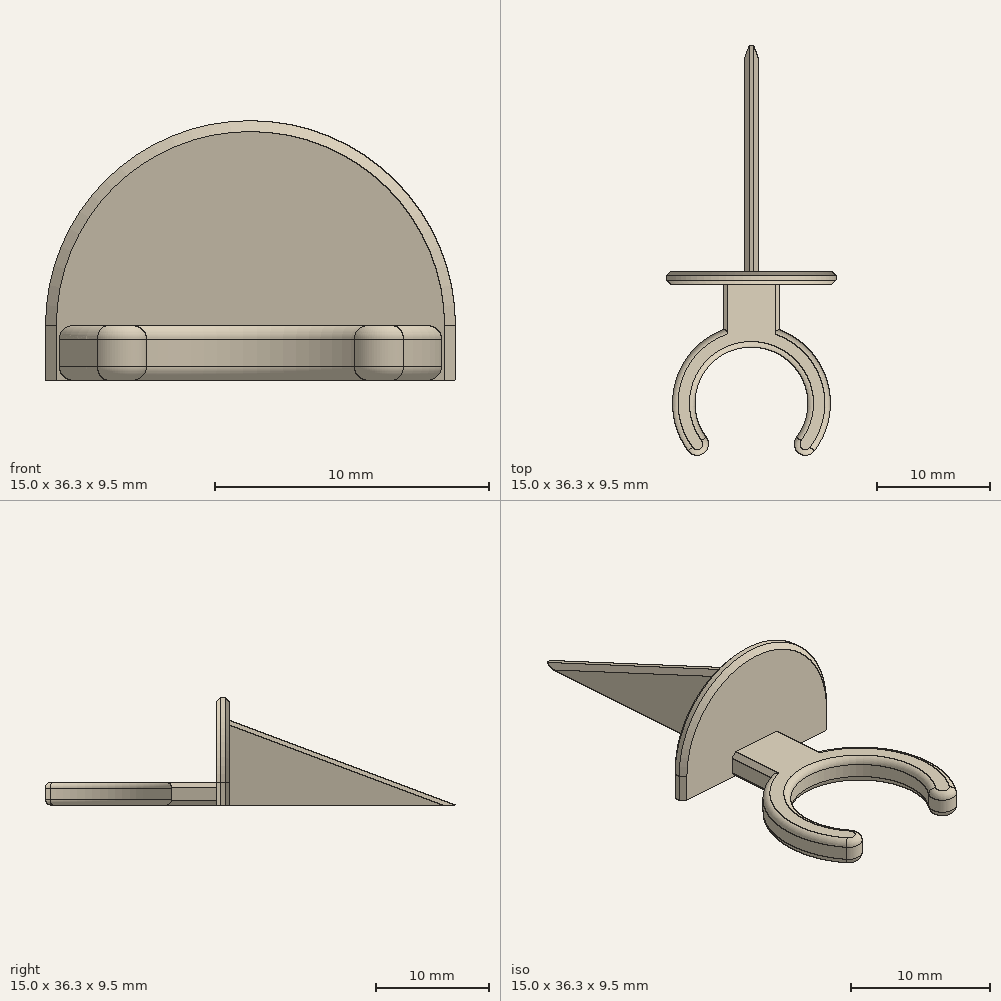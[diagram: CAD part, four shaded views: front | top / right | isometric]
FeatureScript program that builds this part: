
annotation { "Feature Type Name" : "Feature", "Feature Type Description" : "" }
export const myFeature = defineFeature(function(context is Context, id is Id, definition is map)
    precondition{}
    {
        {
            var Q0;
            Q0=qCreatedBy(makeId("Top.planeOp"),FACE);
            var sketch = newSketch(context, id + "F0", { "sketchPlane" : qUnion([Q0])});
            skArc(sketch, "E0", {"start": v(-4, -3) * mm, "mid": v(0, 5) * mm, "end": v(4, -3) * mm});
            skArc(sketch, "E1.0", {"start": v(-5.6, -4.2) * mm, "mid": v(0, 7) * mm, "end": v(5.6, -4.2) * mm});
            skLineSegment(sketch, "E2", {"start": v(0, 0) * mm, "end": v(-4, -3) * mm, "construction": true});
            skLineSegment(sketch, "E3", {"start": v(-4, -3) * mm, "end": v(-5.6, -4.2) * mm, "construction": true});
            skArc(sketch, "E4", {"start": v(-5.6, -4.2) * mm, "mid": v(-4.2, -4.4) * mm, "end": v(-4, -3) * mm});
            skArc(sketch, "E5", {"start": v(4, -3) * mm, "mid": v(4.2, -4.4) * mm, "end": v(5.6, -4.2) * mm});
            skSolve(sketch);
        }
        {
            var Q0;
            Q0=qCreatedBy(makeId("Top.planeOp"),FACE);
            var sketch = newSketch(context, id + "F1", { "sketchPlane" : qUnion([Q0])});
            skLineSegment(sketch, "E6.bottom", {"start": v(2.5, 6.54) * mm, "end": v(-2.5, 6.54) * mm});
            skLineSegment(sketch, "E6.top", {"start": v(2.5, 10.54) * mm, "end": v(-2.5, 10.54) * mm});
            skLineSegment(sketch, "E6.left", {"start": v(2.5, 6.54) * mm, "end": v(2.5, 10.54) * mm});
            skLineSegment(sketch, "E6.right", {"start": v(-2.5, 6.54) * mm, "end": v(-2.5, 10.54) * mm});
            skPoint(sketch, "E6.middle", {"position": v(0, 8.54) * mm});
            skLineSegment(sketch, "E7.bottom", {"start": v(7.5, 10.54) * mm, "end": v(-7.5, 10.54) * mm});
            skLineSegment(sketch, "E7.top", {"start": v(7.5, 11.74) * mm, "end": v(-7.5, 11.74) * mm});
            skLineSegment(sketch, "E7.left", {"start": v(7.5, 10.54) * mm, "end": v(7.5, 11.74) * mm});
            skLineSegment(sketch, "E7.right", {"start": v(-7.5, 10.54) * mm, "end": v(-7.5, 11.74) * mm});
            skPoint(sketch, "E7.middle", {"position": v(0, 11.14) * mm});
            skSolve(sketch);
        }
        {
            var Q0;
            Q0 = qSketchRegion(id + "F0", true);
            var Q1;
            Q1 = qSketchRegion(id + "F1", true);
            extrude(context, id + "F2", {"entities" : qUnion([Q0, Q1]), "depth" : 2 * mm, "offsetDistance" : 25 * mm});
        }
        {
            var Q0;
            Q0=makeQuery(id+"F2.opExtrude","SWEPT_BODY",BODY,{"disambiguationData":[OSD([sQuery(id+"F1.wireOp",EDGE,"E6.bottom"),sQuery(id+"F1.wireOp",EDGE,"E6.left"),sQuery(id+"F1.wireOp",EDGE,"E6.right"),sQuery(id+"F1.wireOp",EDGE,"E7.bottom"),sQuery(id+"F1.wireOp",EDGE,"E7.top"),sQuery(id+"F1.wireOp",EDGE,"E7.left"),sQuery(id+"F1.wireOp",EDGE,"E7.right")])]});
            var Q1;
            Q1=makeQuery(id+"F2.opExtrude","SWEPT_BODY",BODY,{"disambiguationData":[OSD([sQuery(id+"F0.wireOp",EDGE,"E0"),sQuery(id+"F0.wireOp",EDGE,"E1.0"),sQuery(id+"F0.wireOp",EDGE,"E4"),sQuery(id+"F0.wireOp",EDGE,"E5")])]});
            booleanBodies(context, id + "F3", {"operationType" : BooleanOperationType.UNION, "tools" : qUnion([Q0, Q1])});
        }
        {
            var Q0;
            Q0=makeQuery(id+"F2.opExtrude","SWEPT_FACE",FACE,{"disambiguationData":[OSD([sQuery(id+"F1.wireOp",EDGE,"E7.top")])]});
            var sketch = newSketch(context, id + "F4", { "sketchPlane" : qUnion([Q0])});
            skLineSegment(sketch, "E8.0", {"start": v(-7.5, 2) * mm, "end": v(-7.5, 0) * mm});
            skLineSegment(sketch, "E8.1", {"start": v(-7.5, 0) * mm, "end": v(7.5, 0) * mm});
            skLineSegment(sketch, "E8.2", {"start": v(7.5, 2) * mm, "end": v(7.5, 0) * mm});
            skArc(sketch, "E9", {"start": v(-7.5, 2) * mm, "mid": v(0, 9.5) * mm, "end": v(7.5, 2) * mm});
            skSolve(sketch);
        }
        {
            var Q0;
            Q0 = qSketchRegion(id + "F4", true);
            var Q1;
            {var subQ0=sQuery(id+"F1.wireOp",EDGE,"E7.bottom");Q1=makeQuery(id+"F2.opExtrude","SWEPT_FACE",FACE,{"disambiguationData":[OSD([subQ0]),TDD([makeQuery(id+"F1.imprint","IMPRINT",EDGE,{"disambiguationData":[TD([[makeQuery(id+"F1.imprint","INTERSECT",VERTEX,{"derivedFrom":[sQuery(id+"F1.wireOp",EDGE,"E6.left"),subQ0]}),1.0]])],"derivedFrom":subQ0})])]});}
            extrude(context, id + "F5", {"entities" : qUnion([Q0]), "operationType" : NewBodyOperationType.ADD, "endBound" : BoundingType.UP_TO_SURFACE, "oppositeDirection" : true, "depth" : 25 * mm, "endBoundEntityFace" : qUnion([Q1]), "offsetDistance" : 25 * mm});
        }
        {
            var Q0;
            Q0=qCreatedBy(makeId("Right.planeOp"),FACE);
            var sketch = newSketch(context, id + "F6", { "sketchPlane" : qUnion([Q0])});
            skLineSegment(sketch, "E10", {"start": v(11.74, 9.5) * mm, "end": v(11.74, 7.5) * mm, "construction": true});
            skLineSegment(sketch, "E11", {"start": v(11.74, 0) * mm, "end": v(31.74, 0) * mm});
            skLineSegment(sketch, "E12", {"start": v(31.74, 0) * mm, "end": v(11.74, 7.5) * mm});
            skLineSegment(sketch, "E13", {"start": v(11.74, 7.5) * mm, "end": v(11.74, 0) * mm});
            skSolve(sketch);
        }
        {
            var Q0;
            Q0 = qSketchRegion(id + "F6", true);
            extrude(context, id + "F7", {"entities" : qUnion([Q0]), "operationType" : NewBodyOperationType.ADD, "depth" : 0.6 * mm, "offsetDistance" : 25 * mm, "hasSecondDirection" : true, "secondDirectionOppositeDirection" : true, "secondDirectionDepth" : 0.6 * mm});
        }
        {
            var Q0;
            Q0=makeQuery(id+"F2.opExtrude","CAP_EDGE",EDGE,{"disambiguationData":[OSD([sQuery(id+"F0.wireOp",EDGE,"E4")])],"isStart":false});
            var Q1;
            Q1=makeQuery(id+"F2.opExtrude","CAP_EDGE",EDGE,{"disambiguationData":[OSD([sQuery(id+"F0.wireOp",EDGE,"E0")])],"isStart":false});
            var Q2;
            {var subQ0=sQuery(id+"F0.wireOp",EDGE,"E4");var subQ2=sQuery(id+"F0.wireOp",EDGE,"E1.0");Q2=makeQuery(id+"F3.opBoolean","SPLIT",EDGE,{"disambiguationData":[TD([makeQuery(id+"F2.opExtrude","SWEPT_FACE",FACE,{"disambiguationData":[OSD([subQ0])]})])],"derivedFrom":makeQuery(id+"F2.opExtrude","CAP_EDGE",EDGE,{"disambiguationData":[OSD([subQ2])],"isStart":false})});}
            var Q3;
            {var subQ0=sQuery(id+"F0.wireOp",EDGE,"E5");var subQ2=sQuery(id+"F0.wireOp",EDGE,"E1.0");Q3=makeQuery(id+"F3.opBoolean","SPLIT",EDGE,{"disambiguationData":[TD([makeQuery(id+"F2.opExtrude","SWEPT_FACE",FACE,{"disambiguationData":[OSD([subQ0])]})])],"derivedFrom":makeQuery(id+"F2.opExtrude","CAP_EDGE",EDGE,{"disambiguationData":[OSD([subQ2])],"isStart":false})});}
            var Q4;
            Q4=makeQuery(id+"F2.opExtrude","CAP_EDGE",EDGE,{"disambiguationData":[OSD([sQuery(id+"F0.wireOp",EDGE,"E5")])],"isStart":false});
            var Q5;
            Q5=makeQuery(id+"F2.opExtrude","CAP_EDGE",EDGE,{"disambiguationData":[OSD([sQuery(id+"F0.wireOp",EDGE,"E5")])],"isStart":true});
            var Q6;
            Q6=makeQuery(id+"F2.opExtrude","CAP_EDGE",EDGE,{"disambiguationData":[OSD([sQuery(id+"F0.wireOp",EDGE,"E4")])],"isStart":true});
            var Q7;
            Q7=makeQuery(id+"F2.opExtrude","CAP_EDGE",EDGE,{"disambiguationData":[OSD([sQuery(id+"F0.wireOp",EDGE,"E0")])],"isStart":true});
            var Q8;
            {var subQ1=sQuery(id+"F0.wireOp",EDGE,"E5");var subQ2=sQuery(id+"F0.wireOp",EDGE,"E1.0");Q8=makeQuery(id+"F3.opBoolean","SPLIT",EDGE,{"disambiguationData":[TD([makeQuery(id+"F2.opExtrude","SWEPT_FACE",FACE,{"disambiguationData":[OSD([subQ1])]})])],"derivedFrom":makeQuery(id+"F2.opExtrude","CAP_EDGE",EDGE,{"disambiguationData":[OSD([subQ2])],"isStart":true})});}
            var Q9;
            {var subQ1=sQuery(id+"F0.wireOp",EDGE,"E4");var subQ2=sQuery(id+"F0.wireOp",EDGE,"E1.0");Q9=makeQuery(id+"F3.opBoolean","SPLIT",EDGE,{"disambiguationData":[TD([makeQuery(id+"F2.opExtrude","SWEPT_FACE",FACE,{"disambiguationData":[OSD([subQ1])]})])],"derivedFrom":makeQuery(id+"F2.opExtrude","CAP_EDGE",EDGE,{"disambiguationData":[OSD([subQ2])],"isStart":true})});}
            fillet(context, id + "F8", {"entities" : qUnion([Q0, Q1, Q2, Q3, Q4, Q5, Q6, Q7, Q8, Q9]), "radius" : 0.5 * mm, "tangentPropagation" : true, "allowEdgeOverflow" : false});
        }
        {
            var Q0;
            Q0=makeQuery(id+"F2.opExtrude","CAP_EDGE",EDGE,{"disambiguationData":[OSD([sQuery(id+"F1.wireOp",EDGE,"E6.left")])],"isStart":false});
            var Q1;
            Q1=makeQuery(id+"F2.opExtrude","CAP_EDGE",EDGE,{"disambiguationData":[OSD([sQuery(id+"F1.wireOp",EDGE,"E6.right")])],"isStart":false});
            var Q2;
            Q2=makeQuery(id+"F2.opExtrude","CAP_EDGE",EDGE,{"disambiguationData":[OSD([sQuery(id+"F1.wireOp",EDGE,"E6.left")])],"isStart":true});
            var Q3;
            Q3=makeQuery(id+"F2.opExtrude","CAP_EDGE",EDGE,{"disambiguationData":[OSD([sQuery(id+"F1.wireOp",EDGE,"E6.right")])],"isStart":true});
            var Q4;
            Q4=makeQuery(id+"F2.opExtrude","SWEPT_EDGE",EDGE,{"disambiguationData":[OSD([sQuery(id+"F1.wireOp",EDGE,"E7.bottom"),sQuery(id+"F1.wireOp",EDGE,"E7.left")])]});
            var Q5;
            Q5=makeQuery(id+"F5.opExtrude","CAP_EDGE",EDGE,{"disambiguationData":[OSD([sQuery(id+"F4.wireOp",EDGE,"E9")])],"isStart":false});
            var Q6;
            Q6=makeQuery(id+"F2.opExtrude","SWEPT_EDGE",EDGE,{"disambiguationData":[OSD([sQuery(id+"F1.wireOp",EDGE,"E7.bottom"),sQuery(id+"F1.wireOp",EDGE,"E7.right")])]});
            var Q7;
            Q7=makeQuery(id+"F2.opExtrude","SWEPT_EDGE",EDGE,{"disambiguationData":[OSD([sQuery(id+"F1.wireOp",EDGE,"E7.top"),sQuery(id+"F1.wireOp",EDGE,"E7.left")])]});
            var Q8;
            Q8=makeQuery(id+"F5.opExtrude","CAP_EDGE",EDGE,{"disambiguationData":[OSD([sQuery(id+"F4.wireOp",EDGE,"E9")])],"isStart":true});
            var Q9;
            Q9=makeQuery(id+"F2.opExtrude","SWEPT_EDGE",EDGE,{"disambiguationData":[OSD([sQuery(id+"F1.wireOp",EDGE,"E7.top"),sQuery(id+"F1.wireOp",EDGE,"E7.right")])]});
            var Q10;
            Q10=makeQuery(id+"F7.opExtrude","CAP_EDGE",EDGE,{"disambiguationData":[OSD([sQuery(id+"F6.wireOp",EDGE,"E12")])],"isStart":true});
            var Q11;
            Q11=makeQuery(id+"F7.opExtrude","CAP_EDGE",EDGE,{"disambiguationData":[OSD([sQuery(id+"F6.wireOp",EDGE,"E12")])],"isStart":false});
            chamfer(context, id + "F9", {"entities" : qUnion([Q0, Q1, Q2, Q3, Q4, Q5, Q6, Q7, Q8, Q9, Q10, Q11]), "width" : 0.4 * mm, "tangentPropagation" : true});
        }
    });
